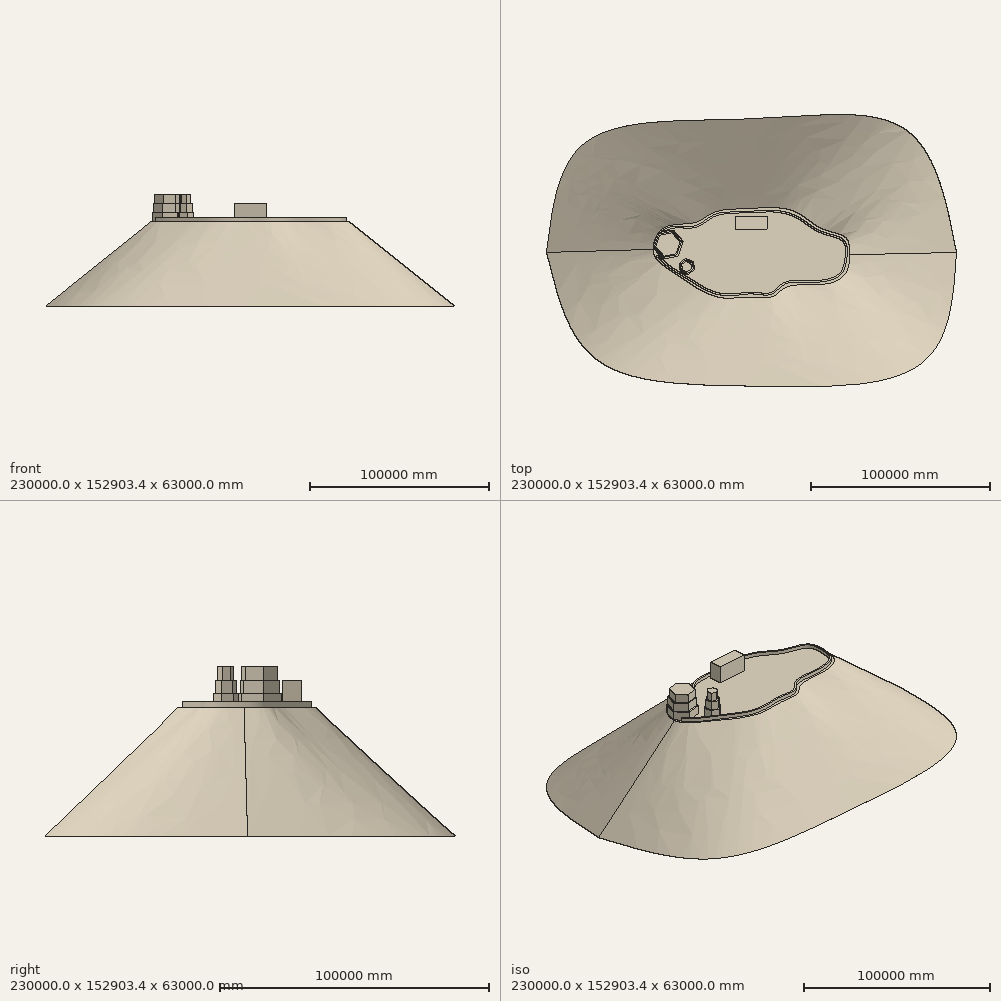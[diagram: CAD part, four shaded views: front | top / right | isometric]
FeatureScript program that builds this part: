
annotation { "Feature Type Name" : "Feature", "Feature Type Description" : "" }
export const myFeature = defineFeature(function(context is Context, id is Id, definition is map)
    precondition{}
    {
        {
            var Q0;
            Q0=qCreatedBy(makeId("Top.planeOp"),FACE);
            var sketch = newSketch(context, id + "F0", { "sketchPlane" : qUnion([Q0])});
            skFitSpline(sketch, "E0", {"points": [v(-115000, 0) * mm, v(-93084.68, 61512.1) * mm, v(0, 75000) * mm, v(86370.97, 68951.61) * mm, v(115000, 0) * mm], "startDerivative": vector(39435.94, 326168.34) * mm, "endDerivative": vector(68602.5, -351904.63) * mm});
            skFitSpline(sketch, "E1", {"points": [v(-115000, 0) * mm, v(-87459.68, -59697.58) * mm, v(0, -75000) * mm, v(96532.26, -61512.1) * mm, v(115000, 0) * mm], "startDerivative": vector(74357.8, -308446.07) * mm, "endDerivative": vector(20026.61, 322600.8) * mm});
            skSolve(sketch);
        }
        {
            var Q0;
            Q0=qCreatedBy(makeId("Top.planeOp"),FACE);
            cPlane(context, id + "F1", {"entities" : qUnion([Q0]), "cplaneType" : CPlaneType.OFFSET, "offset" : 48000 * mm, "width" : 150 * mm, "height" : 150 * mm});
        }
        {
            var Q0;
            Q0=qCreatedBy(id+"F1.planeOp",FACE);
            var sketch = newSketch(context, id + "F2", { "sketchPlane" : qUnion([Q0])});
            skFitSpline(sketch, "E2", {"points": [v(-55000, 0) * mm, v(-49195.48, 13593.62) * mm, v(-31440.72, 16737.7) * mm, v(-21638.61, 22101.1) * mm, v(0, 25000) * mm, v(24042.9, 23025.84) * mm, v(39023.49, 13593.62) * mm, v(52894.4, 8230.2) * mm, v(55000, 0) * mm, v(53449.23, -10819.18) * mm, v(43092.29, -17477.21) * mm, v(20159.05, -19326.67) * mm, v(12391.34, -24690.08) * mm, v(0, -25000) * mm, v(-19049.38, -25000) * mm, v(-45126.69, -10449.29) * mm, v(-55000, 0) * mm]});
            skSolve(sketch);
        }
        {
            var Q0;
            Q0=makeQuery(id+"F2.imprint","IMPRINT",FACE,{"disambiguationData":[TD([[makeQuery(id+"F2.imprint","IMPRINT",EDGE,{"derivedFrom":sQuery(id+"F2.wireOp",EDGE,"E2")}),-1.0]])]});
            var Q1;
            Q1=makeQuery(id+"F0.imprint","IMPRINT",FACE,{"disambiguationData":[TD([[makeQuery(id+"F0.imprint","IMPRINT",EDGE,{"derivedFrom":sQuery(id+"F0.wireOp",EDGE,"E0")}),-1.0]])]});
            loft(context, id + "F3", {"sheetProfilesArray" : [{ "sheetProfileEntities" : qUnion([Q0]) }, { "sheetProfileEntities" : qUnion([Q1]) }]});
        }
        {
            var Q0;
            Q0=makeQuery(id+"F3.opLoft","CAP_FACE",FACE,{"disambiguationData":[OSD([makeQuery(id+"F2.imprint","IMPRINT",FACE,{"disambiguationData":[TD([[makeQuery(id+"F2.imprint","IMPRINT",EDGE,{"derivedFrom":sQuery(id+"F2.wireOp",EDGE,"E2")}),-1.0]])]})])],"isStart":true});
            var sketch = newSketch(context, id + "F4", { "sketchPlane" : qUnion([Q0])});
            skLineSegment(sketch, "E3", {"start": v(-54550.48, 6198.7) * mm, "end": v(-46752.04, 4414.26) * mm});
            skCircle(sketch, "E4.cCircle", {"center": v(-46752.04, 4414.26) * mm, "radius": 7500 * mm, "construction": true});
            skLineSegment(sketch, "E4.0", {"start": v(-38242.25, 6021.6) * mm, "end": v(-41105.15, -2151.77) * mm});
            skLineSegment(sketch, "E4.1", {"start": v(-41105.15, -2151.77) * mm, "end": v(-49614.94, -3759.1) * mm});
            skLineSegment(sketch, "E4.2", {"start": v(-49614.94, -3759.1) * mm, "end": v(-55261.83, 2806.92) * mm});
            skLineSegment(sketch, "E4.3", {"start": v(-55261.83, 2806.92) * mm, "end": v(-52398.92, 10980.28) * mm});
            skLineSegment(sketch, "E4.4", {"start": v(-52398.92, 10980.28) * mm, "end": v(-43889.14, 12587.62) * mm});
            skLineSegment(sketch, "E4.5", {"start": v(-43889.14, 12587.62) * mm, "end": v(-38242.25, 6021.6) * mm});
            skPoint(sketch, "E4.0.midPoint", {"position": v(-39673.7, 1934.91) * mm});
            skSolve(sketch);
        }
        {
            var Q0;
            Q0=makeQuery(id+"F4.imprint","IMPRINT",FACE,{"disambiguationData":[TD([[makeQuery(id+"F4.imprint","IMPRINT",EDGE,{"derivedFrom":sQuery(id+"F4.wireOp",EDGE,"E4.0")}),-1.0]])]});
            extrude(context, id + "F5", {"entities" : qUnion([Q0]), "operationType" : NewBodyOperationType.ADD, "depth" : 5000 * mm});
        }
        {
            var Q0;
            Q0=makeQuery(id+"F5.opExtrude","CAP_FACE",FACE,{"disambiguationData":[OSD([sQuery(id+"F0.wireOp",EDGE,"E0"),sQuery(id+"F0.wireOp",EDGE,"E1"),sQuery(id+"F2.wireOp",EDGE,"E2"),sQuery(id+"F4.wireOp",EDGE,"E4.0"),sQuery(id+"F4.wireOp",EDGE,"E4.1"),sQuery(id+"F4.wireOp",EDGE,"E4.2"),sQuery(id+"F4.wireOp",EDGE,"E4.3"),sQuery(id+"F4.wireOp",EDGE,"E4.4"),sQuery(id+"F4.wireOp",EDGE,"E4.5")])],"isStart":false});
            var sketch = newSketch(context, id + "F6", { "sketchPlane" : qUnion([Q0])});
            skCircle(sketch, "E5.cCircle", {"center": v(-46880.17, 4500.61) * mm, "radius": 6688.06 * mm, "construction": true});
            skLineSegment(sketch, "E5.0", {"start": v(-54478.4, 3119.6) * mm, "end": v(-51875.28, 10390.35) * mm});
            skLineSegment(sketch, "E5.1", {"start": v(-51875.28, 10390.35) * mm, "end": v(-44277.06, 11771.37) * mm});
            skLineSegment(sketch, "E5.2", {"start": v(-44277.06, 11771.37) * mm, "end": v(-39281.95, 5881.63) * mm});
            skLineSegment(sketch, "E5.3", {"start": v(-39281.95, 5881.63) * mm, "end": v(-41885.06, -1389.13) * mm});
            skLineSegment(sketch, "E5.4", {"start": v(-41885.06, -1389.13) * mm, "end": v(-49483.28, -2770.15) * mm});
            skLineSegment(sketch, "E5.5", {"start": v(-49483.28, -2770.15) * mm, "end": v(-54478.4, 3119.6) * mm});
            skPoint(sketch, "E5.0.midPoint", {"position": v(-53176.84, 6754.97) * mm});
            skSolve(sketch);
        }
        {
            var Q0;
            Q0=makeQuery(id+"F6.imprint","IMPRINT",FACE,{"disambiguationData":[TD([[makeQuery(id+"F6.imprint","IMPRINT",EDGE,{"derivedFrom":sQuery(id+"F6.wireOp",EDGE,"E5.0")}),-1.0]])]});
            extrude(context, id + "F7", {"entities" : qUnion([Q0]), "operationType" : NewBodyOperationType.ADD, "depth" : 5000 * mm});
        }
        {
            var Q0;
            Q0=makeQuery(id+"F7.opExtrude","CAP_FACE",FACE,{"disambiguationData":[OSD([sQuery(id+"F6.wireOp",EDGE,"E5.0"),sQuery(id+"F6.wireOp",EDGE,"E5.1"),sQuery(id+"F6.wireOp",EDGE,"E5.2"),sQuery(id+"F6.wireOp",EDGE,"E5.3"),sQuery(id+"F6.wireOp",EDGE,"E5.4"),sQuery(id+"F6.wireOp",EDGE,"E5.5")])],"isStart":false});
            var sketch = newSketch(context, id + "F8", { "sketchPlane" : qUnion([Q0])});
            skCircle(sketch, "E6.cCircle", {"center": v(-46796.6, 4410.22) * mm, "radius": 6040.92 * mm, "construction": true});
            skLineSegment(sketch, "E6.0", {"start": v(-51393, 9657.15) * mm, "end": v(-44550.83, 11014.27) * mm});
            skLineSegment(sketch, "E6.1", {"start": v(-44550.83, 11014.27) * mm, "end": v(-39954.44, 5767.34) * mm});
            skLineSegment(sketch, "E6.2", {"start": v(-39954.44, 5767.34) * mm, "end": v(-42200.22, -836.7) * mm});
            skLineSegment(sketch, "E6.3", {"start": v(-42200.22, -836.7) * mm, "end": v(-49042.39, -2193.83) * mm});
            skLineSegment(sketch, "E6.4", {"start": v(-49042.39, -2193.83) * mm, "end": v(-53638.77, 3053.1) * mm});
            skLineSegment(sketch, "E6.5", {"start": v(-53638.77, 3053.1) * mm, "end": v(-51393, 9657.15) * mm});
            skPoint(sketch, "E6.0.midPoint", {"position": v(-47971.91, 10335.7) * mm});
            skSolve(sketch);
        }
        {
            var Q0;
            {var subQ0=sQuery(id+"F2.wireOp",EDGE,"E2");var subQ1=makeQuery(id+"F2.imprint","IMPRINT",EDGE,{"derivedFrom":subQ0});Q0=makeQuery(id+"F5.boolean.opBoolean","SPLIT",FACE,{"disambiguationData":[TD([makeQuery(id+"F5.opExtrude","SWEPT_FACE",FACE,{"disambiguationData":[OSD([sQuery(id+"F4.wireOp",EDGE,"E4.0")])]})])],"derivedFrom":makeQuery(id+"F3.opLoft","CAP_FACE",FACE,{"disambiguationData":[OSD([makeQuery(id+"F2.imprint","IMPRINT",FACE,{"disambiguationData":[TD([[subQ1,-1.0]])]})])],"isStart":true})});}
            var sketch = newSketch(context, id + "F9", { "sketchPlane" : qUnion([Q0])});
            skPoint(sketch, "E7.0.internal.snap0", {"position": v(-47955.39, 11819.58) * mm});
            skFitSpline(sketch, "E7", {"points": [v(-51090.18, 11819.58) * mm, v(-45135.25, 14330.4) * mm, v(-38003.08, 14696.04) * mm, v(-30275.62, 15385.9) * mm, v(-21578.99, 20754.82) * mm, v(-11237.18, 22930.05) * mm, v(4464.42, 23551.87) * mm, v(15659.1, 23396.88) * mm, v(26853.06, 19665.5) * mm, v(34781.74, 14145.25) * mm, v(42400.23, 10802.7) * mm, v(50252.3, 8083.85) * mm, v(53518.6, 3495.47) * mm, v(52973.57, -6376.8) * mm, v(49708.45, -12986.25) * mm, v(39213.22, -16561.05) * mm, v(28252.34, -16560.04) * mm, v(18612.73, -18035.92) * mm, v(13250, -22469.3) * mm, v(8040.3, -23946.46) * mm, v(0, -23245.23) * mm, v(-6185.77, -23867.9) * mm, v(-17612.52, -23868.43) * mm, v(-28573.08, -19514.87) * mm, v(-35958.38, -14850.08) * mm, v(-45018.89, -9321) * mm, v(-53569.9, -2091.5) * mm], "startDerivative": vector(158396.75, 66508.43) * mm, "endDerivative": vector(-197831.18, 185301.4) * mm});
            skFitSpline(sketch, "E8.0", {"points": [v(-50703.04, 10897.56) * mm, v(-50593.48, 10943.56) * mm, v(-50373.3, 11038.71) * mm, v(-50039.51, 11189.33) * mm, v(-49702.07, 11346.38) * mm, v(-49360.94, 11508.37) * mm, v(-49016.19, 11673.88) * mm, v(-48667.98, 11841.43) * mm, v(-48316.53, 12009.58) * mm, v(-47962.14, 12176.9) * mm, v(-47605.14, 12341.9) * mm, v(-47245.93, 12503.18) * mm, v(-46884.93, 12659.29) * mm, v(-46522.62, 12808.8) * mm, v(-46220, 12926.73) * mm, v(-45977.77, 13016.39) * mm, v(-45796.1, 13081.12) * mm, v(-45614.5, 13143.18) * mm, v(-45463.27, 13192.52) * mm, v(-45342.4, 13230.5) * mm, v(-45251.8, 13258.2) * mm, v(-45161.27, 13285.13) * mm, v(-45085.9, 13306.89) * mm, v(-45025.65, 13323.88) * mm, v(-44980.49, 13336.41) * mm, v(-44935.35, 13348.74) * mm, v(-44897.75, 13358.83) * mm, v(-44867.69, 13366.8) * mm, v(-44837.6, 13374.7) * mm, v(-44799.97, 13384.45) * mm, v(-44754.76, 13395.95) * mm, v(-44694.4, 13411.04) * mm, v(-44618.82, 13429.43) * mm, v(-44527.9, 13450.73) * mm, v(-44436.77, 13471.3) * mm, v(-44314.96, 13497.73) * mm, v(-44162.14, 13528.96) * mm, v(-43977.85, 13563.63) * mm, v(-43792.63, 13595.55) * mm, v(-43544.43, 13634.57) * mm, v(-43231.83, 13676.9) * mm, v(-42852.9, 13717.99) * mm, v(-42470.15, 13750.01) * mm, v(-42083.58, 13773.61) * mm, v(-41693.22, 13789.44) * mm, v(-41299.1, 13798.15) * mm, v(-40901.31, 13800.43) * mm, v(-40499.89, 13796.95) * mm, v(-40094.9, 13788.43) * mm, v(-39686.43, 13775.57) * mm, v(-39343.2, 13761.85) * mm, v(-39066.94, 13749.43) * mm, v(-38858.92, 13739.5) * mm, v(-38650.08, 13729.04) * mm, v(-38475.37, 13719.96) * mm, v(-38335.2, 13712.52) * mm, v(-38229.89, 13706.87) * mm, v(-38141.95, 13702.11) * mm, v(-38071.5, 13698.28) * mm, v(-38001, 13694.44) * mm, v(-37912.69, 13689.6) * mm, v(-37771.06, 13681.86) * mm, v(-37593.4, 13672.16) * mm, v(-37379.22, 13660.69) * mm, v(-37164.09, 13649.52) * mm, v(-36948.02, 13638.82) * mm, v(-36658.7, 13625.38) * mm, v(-36294.83, 13610.53) * mm, v(-35854.78, 13597.11) * mm, v(-35411.5, 13589.41) * mm, v(-34965.12, 13588.76) * mm, v(-34515.84, 13596.52) * mm, v(-34063.83, 13614.06) * mm, v(-33609.28, 13642.8) * mm, v(-33152.43, 13684.15) * mm, v(-32693.53, 13739.56) * mm, v(-32232.89, 13810.48) * mm, v(-31847.86, 13883.72) * mm, v(-31539.35, 13951.5) * mm, v(-31307.78, 14007.13) * mm, v(-31076.1, 14067.7) * mm, v(-30844.34, 14133.41) * mm, v(-30651.22, 14192.59) * mm, v(-30496.76, 14242.66) * mm, v(-30380.94, 14281.6) * mm, v(-30265.17, 14321.96) * mm, v(-30168.73, 14356.77) * mm, v(-30091.6, 14385.35) * mm, v(-30033.78, 14407.15) * mm, v(-29985.6, 14425.62) * mm, v(-29947.07, 14440.58) * mm, v(-29918.18, 14451.9) * mm, v(-29889.29, 14463.3) * mm, v(-29850.81, 14478.62) * mm, v(-29802.79, 14497.97) * mm, v(-29745.27, 14521.52) * mm, v(-29668.74, 14553.35) * mm, v(-29573.34, 14593.93) * mm, v(-29459.3, 14643.86) * mm, v(-29345.67, 14694.98) * mm, v(-29194.72, 14764.7) * mm, v(-29007.04, 14854.64) * mm, v(-28783.35, 14966.8) * mm, v(-28561.12, 15082.9) * mm, v(-28340.25, 15202.71) * mm, v(-28047.48, 15367.04) * mm, v(-27684.57, 15580.42) * mm, v(-27253.35, 15847.28) * mm, v(-26825.88, 16123.04) * mm, v(-26401.68, 16405.85) * mm, v(-25980.3, 16693.88) * mm, v(-25561.36, 16985.3) * mm, v(-25144.51, 17278.32) * mm, v(-24729.46, 17571.15) * mm, v(-24315.95, 17861.99) * mm, v(-23903.76, 18149.06) * mm, v(-23492.75, 18430.6) * mm, v(-23082.76, 18704.83) * mm, v(-22741.9, 18925.81) * mm, v(-22469.66, 19097.22) * mm, v(-22265.7, 19222.86) * mm, v(-22061.98, 19345.39) * mm, v(-21858.48, 19464.59) * mm, v(-21689.09, 19560.98) * mm, v(-21553.7, 19636.23) * mm, v(-21452.2, 19691.7) * mm, v(-21350.78, 19746.2) * mm, v(-21266.31, 19790.78) * mm, v(-21198.77, 19825.92) * mm, v(-21148.12, 19852.02) * mm, v(-21097.5, 19877.85) * mm, v(-21046.82, 19903.45) * mm, v(-20996.1, 19928.82) * mm, v(-20928.4, 19962.34) * mm, v(-20809.77, 20020.2) * mm, v(-20639.76, 20100.62) * mm, v(-20434.86, 20193.6) * mm, v(-20229, 20283.15) * mm, v(-20022.1, 20369.38) * mm, v(-19744.8, 20480) * mm, v(-19395.26, 20610.39) * mm, v(-18970.69, 20754.85) * mm, v(-18540.5, 20887.97) * mm, v(-18104.21, 21010.35) * mm, v(-17661.4, 21122.61) * mm, v(-17211.62, 21225.35) * mm, v(-16754.5, 21319.16) * mm, v(-16289.65, 21404.63) * mm, v(-15816.74, 21482.36) * mm, v(-15335.43, 21552.94) * mm, v(-14845.4, 21616.97) * mm, v(-14346.36, 21675.07) * mm, v(-13838.02, 21727.84) * mm, v(-13320.1, 21775.92) * mm, v(-12880.32, 21812.6) * mm, v(-12523.43, 21840.23) * mm, v(-12253.21, 21860.18) * mm, v(-11980.4, 21879.44) * mm, v(-11750.88, 21894.98) * mm, v(-11565.93, 21907.14) * mm, v(-11426.55, 21916.15) * mm, v(-11309.85, 21923.55) * mm, v(-11216.15, 21929.43) * mm, v(-11122.22, 21935.28) * mm, v(-11004.42, 21942.52) * mm, v(-10862.46, 21951.12) * mm, v(-10719.9, 21959.62) * mm, v(-10529.05, 21970.84) * mm, v(-10289.07, 21984.63) * mm, v(-9998.9, 22000.82) * mm, v(-9706.66, 22016.67) * mm, v(-9314.35, 22037.34) * mm, v(-8819.22, 22062.37) * mm, v(-8218.23, 22091.18) * mm, v(-7611.17, 22118.84) * mm, v(-6998.78, 22145.44) * mm, v(-6176.16, 22179.6) * mm, v(-5138.3, 22220.04) * mm, v(-3883.52, 22265.62) * mm, v(-2625.3, 22308.93) * mm, v(-1369.55, 22350.63) * mm, v(-330.07, 22384.6) * mm, v(494.4, 22411.62) * mm, v(1108.45, 22431.91) * mm, v(1717.48, 22452.3) * mm, v(2320.76, 22472.87) * mm, v(2818.1, 22490.24) * mm, v(3212.36, 22504.3) * mm, v(3506.17, 22514.96) * mm, v(3798, 22525.72) * mm, v(4039.45, 22534.79) * mm, v(4231.54, 22542.1) * mm, v(4351.13, 22546.71) * mm, v(4446.53, 22550.41) * mm, v(4517.93, 22553.2) * mm, v(4589.18, 22555.99) * mm, v(4683.97, 22559.72) * mm, v(4802.06, 22564.4) * mm, v(4990.18, 22571.92) * mm, v(5317.26, 22585.12) * mm, v(5778.58, 22603.95) * mm, v(6323.26, 22626.06) * mm, v(6859.6, 22647.23) * mm, v(7388.16, 22667.02) * mm, v(8083.31, 22690.95) * mm, v(8935.73, 22715.18) * mm, v(9936.94, 22731.67) * mm, v(10921.3, 22732.13) * mm, v(11893.83, 22713.17) * mm, v(12698.7, 22678.38) * mm, v(13341.88, 22637.47) * mm, v(13824.6, 22599.83) * mm, v(14308.33, 22554.8) * mm, v(14712.85, 22510.76) * mm, v(14997.06, 22476.32) * mm, v(15159.8, 22455.58) * mm, v(15282.05, 22439.5) * mm, v(15384.08, 22425.63) * mm, v(15465.8, 22414.27) * mm, v(15547.6, 22402.72) * mm, v(15650, 22387.93) * mm, v(15773.12, 22369.63) * mm, v(15896.5, 22350.76) * mm, v(16061.28, 22324.86) * mm, v(16267.82, 22291.1) * mm, v(16516.47, 22248.36) * mm, v(16848.95, 22188.43) * mm, v(17266.15, 22108.03) * mm, v(17768.71, 22002.88) * mm, v(18272.58, 21889.15) * mm, v(18945.31, 21726.2) * mm, v(19786.36, 21501.6) * mm, v(20790.89, 21199.46) * mm, v(21619.93, 20921.26) * mm, v(22275.86, 20683.34) * mm, v(22763.54, 20497.33) * mm, v(23246.34, 20303.89) * mm, v(23723.65, 20103.14) * mm, v(24194.84, 19895.23) * mm, v(24581.9, 19716.11) * mm, v(24887.86, 19569.37) * mm, v(25115.43, 19457.61) * mm, v(25341, 19344.17) * mm, v(25564.52, 19229.06) * mm, v(25749, 19131.77) * mm, v(25895.47, 19053.12) * mm, v(26004.75, 18993.73) * mm, v(26113.47, 18933.94) * mm, v(26221.6, 18873.75) * mm, v(26311.22, 18823.26) * mm, v(26382.6, 18782.67) * mm, v(26436.02, 18752.11) * mm, v(26489.33, 18721.44) * mm, v(26560.24, 18680.4) * mm, v(26683.92, 18608.19) * mm, v(26859.47, 18503.94) * mm, v(27068.38, 18377.19) * mm, v(27275.6, 18248.86) * mm, v(27481.2, 18119.03) * mm, v(27753.28, 17944.05) * mm, v(28089.73, 17722) * mm, v(28488.18, 17450.89) * mm, v(28881.92, 17175.8) * mm, v(29271.52, 16897.45) * mm, v(29786.26, 16522.85) * mm, v(30295.05, 16144.49) * mm, v(30800.25, 15765.21) * mm, v(31177.96, 15481.04) * mm, v(31555.1, 15197.88) * mm, v(31932.25, 14916.48) * mm, v(32310.07, 14637.6) * mm, v(32626, 14407.94) * mm, v(32879.7, 14226.25) * mm, v(33070.55, 14091.1) * mm, v(33262.04, 13957.17) * mm, v(33454.25, 13824.55) * mm, v(33647.28, 13693.36) * mm, v(33808.87, 13585.3) * mm, v(33938.64, 13499.67) * mm, v(34036.21, 13435.87) * mm, v(34117.75, 13383.06) * mm, v(34183.11, 13341.04) * mm, v(34224.02, 13314.87) * mm, v(34256.79, 13294) * mm, v(34289.56, 13273.16) * mm, v(34330.56, 13247.2) * mm, v(34379.79, 13216.2) * mm, v(34445.48, 13175.03) * mm, v(34527.7, 13123.9) * mm, v(34626.5, 13063.1) * mm, v(34725.48, 13002.82) * mm, v(34857.64, 12923.15) * mm, v(35023.24, 12824.88) * mm, v(35222.6, 12709) * mm, v(35422.6, 12595.17) * mm, v(35623.26, 12483.32) * mm, v(35891.68, 12336.8) * mm, v(36228.86, 12158.49) * mm, v(36636.2, 11951.94) * mm, v(37046.3, 11752.56) * mm, v(37459.24, 11560.07) * mm, v(37875.08, 11374.19) * mm, v(38433.49, 11134.77) * mm, v(38997.95, 10907.43) * mm, v(39568.78, 10691.01) * mm, v(40000.15, 10533.87) * mm, v(40362.42, 10406.98) * mm, v(40653.95, 10307.76) * mm, v(40873.46, 10234.46) * mm, v(41093.86, 10162.23) * mm, v(41315.14, 10091.04) * mm, v(41537.33, 10020.84) * mm, v(41723.25, 9963.15) * mm, v(41872.45, 9917.46) * mm, v(41965.89, 9889.1) * mm, v(42040.76, 9866.52) * mm, v(42096.97, 9849.63) * mm, v(42153.24, 9832.8) * mm, v(42228.3, 9810.46) * mm, v(42322.22, 9782.66) * mm, v(42472.61, 9738.5) * mm, v(42660.83, 9683.81) * mm, v(42886.92, 9618.94) * mm, v(43113.11, 9554.7) * mm, v(43339.28, 9491.03) * mm, v(43640.63, 9406.72) * mm, v(44016.59, 9302.23) * mm, v(44465.5, 9177.52) * mm, v(44911.11, 9052.76) * mm, v(45352.29, 8927.24) * mm, v(45787.9, 8800.28) * mm, v(46216.82, 8671.22) * mm, v(46637.88, 8539.4) * mm, v(47049.89, 8404.25) * mm, v(47451.65, 8265.18) * mm, v(47841.96, 8121.65) * mm, v(48219.59, 7973.18) * mm, v(48522.7, 7845) * mm, v(48757.63, 7739.59) * mm, v(48929.9, 7659.06) * mm, v(49098.1, 7577.03) * mm, v(49262.08, 7493.47) * mm, v(49395.1, 7422.55) * mm, v(49499.27, 7365.02) * mm, v(49576.25, 7321.48) * mm, v(49639.44, 7284.86) * mm, v(49689.4, 7255.37) * mm, v(49726.59, 7233.15) * mm, v(49763.47, 7210.83) * mm, v(49800.1, 7188.4) * mm, v(49836.46, 7165.83) * mm, v(49884.58, 7135.6) * mm, v(49944.08, 7097.5) * mm, v(50014.43, 7051.3) * mm, v(50083.73, 7004.63) * mm, v(50174.74, 6941.74) * mm, v(50285.93, 6861.9) * mm, v(50458.4, 6731.53) * mm, v(50663.98, 6563.48) * mm, v(50895.18, 6353.33) * mm, v(51111.47, 6134.2) * mm, v(51313.42, 5905.47) * mm, v(51501.61, 5666.38) * mm, v(51676.52, 5416.08) * mm, v(51838.55, 5153.63) * mm, v(51987.97, 4878.04) * mm, v(52102.1, 4636.6) * mm, v(52187.2, 4435.89) * mm, v(52247.9, 4281.47) * mm, v(52305.48, 4123.04) * mm, v(52359.9, 3960.51) * mm, v(52402.62, 3821.56) * mm, v(52435.19, 3708.25) * mm, v(52458.8, 3622.18) * mm, v(52481.62, 3535.01) * mm, v(52499.95, 3461.45) * mm, v(52514.21, 3402.03) * mm, v(52524.7, 3357.2) * mm, v(52534.99, 3312.07) * mm, v(52545.07, 3266.67) * mm, v(52554.94, 3220.96) * mm, v(52567.85, 3159.58) * mm, v(52583.49, 3082.08) * mm, v(52601.45, 2987.86) * mm, v(52624.35, 2860.63) * mm, v(52650.97, 2698.68) * mm, v(52679.75, 2499.87) * mm, v(52705.38, 2296.8) * mm, v(52727.87, 2089.68) * mm, v(52747.26, 1878.72) * mm, v(52769.03, 1592.6) * mm, v(52788.7, 1226.36) * mm, v(52800.59, 774.77) * mm, v(52801.23, 312.65) * mm, v(52791.1, -158.47) * mm, v(52770.7, -637.07) * mm, v(52740.62, -1121.66) * mm, v(52701.38, -1610.78) * mm, v(52653.58, -2102.97) * mm, v(52597.8, -2596.8) * mm, v(52534.65, -3090.87) * mm, v(52464.74, -3583.76) * mm, v(52388.68, -4074.1) * mm, v(52307.1, -4560.48) * mm, v(52235.03, -4961.36) * mm, v(52175.23, -5278.72) * mm, v(52137.03, -5475.54) * mm, v(52106.02, -5631.98) * mm, v(52082.54, -5748.8) * mm, v(52058.86, -5865.05) * mm, v(52038.96, -5961.46) * mm, v(52022.94, -6038.3) * mm, v(52010.88, -6095.77) * mm, v(52000.8, -6143.54) * mm, v(51992.7, -6181.68) * mm, v(51984.6, -6219.75) * mm, v(51974.46, -6267.21) * mm, v(51958.17, -6342.88) * mm, v(51937.72, -6436.94) * mm, v(51913.01, -6549) * mm, v(51879.81, -6697.3) * mm, v(51837.81, -6880.62) * mm, v(51786.48, -7097.26) * mm, v(51734.09, -7310.55) * mm, v(51680.5, -7520.47) * mm, v(51607.33, -7795.85) * mm, v(51512.3, -8131.57) * mm, v(51391.66, -8520.77) * mm, v(51263.52, -8896.26) * mm, v(51127, -9258.1) * mm, v(50981.28, -9606.43) * mm, v(50825.46, -9941.5) * mm, v(50658.67, -10263.63) * mm, v(50479.94, -10573.32) * mm, v(50288.2, -10871.15) * mm, v(50116.6, -11110.01) * mm, v(49971.55, -11295.85) * mm, v(49858.69, -11432.7) * mm, v(49741.57, -11567.1) * mm, v(49620, -11699.15) * mm, v(49514.79, -11807.28) * mm, v(49428.18, -11892.68) * mm, v(49361.98, -11956.2) * mm, v(49294.5, -12019.16) * mm, v(49225.7, -12081.6) * mm, v(49167.27, -12133.2) * mm, v(49119.84, -12174.22) * mm, v(49083.93, -12204.86) * mm, v(49047.67, -12235.36) * mm, v(49011, -12265.78) * mm, v(48973.96, -12296.1) * mm, v(48924.03, -12336.43) * mm, v(48860.66, -12386.59) * mm, v(48783.07, -12446.4) * mm, v(48703.95, -12505.82) * mm, v(48596.46, -12584.51) * mm, v(48458.38, -12681.84) * mm, v(48286.9, -12796.92) * mm, v(48109.8, -12910.21) * mm, v(47927.22, -13021.65) * mm, v(47676.74, -13167.68) * mm, v(47350.84, -13345.3) * mm, v(46940.7, -13550.22) * mm, v(46512.93, -13746.58) * mm, v(46068.98, -13934.16) * mm, v(45610.31, -14112.75) * mm, v(45138.38, -14282.21) * mm, v(44654.62, -14442.41) * mm, v(44160.48, -14593.28) * mm, v(43657.4, -14734.75) * mm, v(43146.8, -14866.77) * mm, v(42630.1, -14989.34) * mm, v(42108.75, -15102.43) * mm, v(41584.12, -15206.07) * mm, v(41057.65, -15300.26) * mm, v(40618.55, -15370.9) * mm, v(40267.75, -15422.71) * mm, v(40005.07, -15459.23) * mm, v(39742.98, -15493.42) * mm, v(39525.22, -15519.96) * mm, v(39351.48, -15540.04) * mm, v(39243.1, -15552.1) * mm, v(39156.55, -15561.46) * mm, v(39070.09, -15570.63) * mm, v(38919.01, -15586.17) * mm, v(38703.82, -15606.96) * mm, v(38446.55, -15629.72) * mm, v(38190.19, -15650.37) * mm, v(37849.51, -15675.17) * mm, v(37425.68, -15701.24) * mm, v(36919.92, -15725.2) * mm, v(36416.6, -15742.38) * mm, v(35915.34, -15753.36) * mm, v(35249.25, -15760.48) * mm, v(34419.92, -15756.67) * mm, v(33427.07, -15736.34) * mm, v(32433.74, -15704.8) * mm, v(31603.28, -15673.08) * mm, v(30935.98, -15646.78) * mm, v(30433.7, -15627.2) * mm, v(29929.3, -15608.37) * mm, v(29506.93, -15593.8) * mm, v(29167.66, -15583.13) * mm, v(28912.48, -15575.69) * mm, v(28656.53, -15568.9) * mm, v(28442.57, -15563.83) * mm, v(28270.99, -15560.18) * mm, v(28099.1, -15556.8) * mm, v(27883.71, -15553.14) * mm, v(27624.5, -15549.72) * mm, v(27364.61, -15547.37) * mm, v(27104.18, -15546.18) * mm, v(26756.34, -15546.28) * mm, v(26320.64, -15549.78) * mm, v(25797.16, -15560.16) * mm, v(25273.82, -15577.5) * mm, v(24751.37, -15602.57) * mm, v(24230.56, -15636.18) * mm, v(23712.14, -15679.14) * mm, v(23196.84, -15732.3) * mm, v(22685.39, -15796.48) * mm, v(22178.51, -15872.6) * mm, v(21676.93, -15961.53) * mm, v(21181.37, -16064.24) * mm, v(20692.59, -16181.7) * mm, v(20211.33, -16314.9) * mm, v(19817.23, -16439.92) * mm, v(19506.54, -16548.88) * mm, v(19275.93, -16635.22) * mm, v(19047.84, -16726.31) * mm, v(18859.98, -16806.3) * mm, v(18711.08, -16872.82) * mm, v(18600.1, -16923.98) * mm, v(18489.87, -16976.44) * mm, v(18398.63, -17021.25) * mm, v(18326.02, -17057.77) * mm, v(18271.75, -17085.49) * mm, v(18217.68, -17113.55) * mm, v(18172.79, -17137.21) * mm, v(18136.97, -17156.32) * mm, v(18101.24, -17175.52) * mm, v(18056.78, -17199.7) * mm, v(18003.72, -17229) * mm, v(17950.97, -17258.56) * mm, v(17898.53, -17288.4) * mm, v(17829, -17328.51) * mm, v(17742.82, -17379.3) * mm, v(17640.58, -17441.22) * mm, v(17539.5, -17504.07) * mm, v(17439.54, -17567.8) * mm, v(17307.76, -17653.9) * mm, v(17145.77, -17763.53) * mm, v(16955.62, -17897.94) * mm, v(16707.51, -18080.53) * mm, v(16407.13, -18314.3) * mm, v(16060.94, -18601.13) * mm, v(15727.66, -18891.9) * mm, v(15405.97, -19184.25) * mm, v(15094.6, -19475.9) * mm, v(14792.36, -19764.65) * mm, v(14498.14, -20048.26) * mm, v(14210.9, -20324.57) * mm, v(13976.62, -20546.95) * mm, v(13791.84, -20719.07) * mm, v(13654.49, -20845.01) * mm, v(13518.3, -20967.55) * mm, v(13383.2, -21086.43) * mm, v(13249.13, -21201.4) * mm, v(13116.03, -21312.26) * mm, v(12983.85, -21418.75) * mm, v(12885.38, -21495.19) * mm, v(12820, -21544.66) * mm, v(12787.35, -21569.1) * mm, v(12754.76, -21593.23) * mm, v(12722.23, -21617.05) * mm, v(12695.15, -21636.65) * mm, v(12673.52, -21652.17) * mm, v(12651.9, -21667.59) * mm, v(12624.85, -21686.7) * mm, v(12592.35, -21709.4) * mm, v(12559.81, -21731.84) * mm, v(12516.38, -21761.44) * mm, v(12461.98, -21797.81) * mm, v(12396.53, -21840.5) * mm, v(12309.02, -21896.12) * mm, v(12199.15, -21963.28) * mm, v(12066.43, -22040.17) * mm, v(11932.74, -22113.46) * mm, v(11753.06, -22206.47) * mm, v(11525.53, -22314.15) * mm, v(11246.94, -22430.2) * mm, v(10961.93, -22533.64) * mm, v(10669.62, -22624.89) * mm, v(10369.19, -22704.29) * mm, v(10059.86, -22772.14) * mm, v(9740.92, -22828.66) * mm, v(9466.62, -22866.5) * mm, v(9241.77, -22891.29) * mm, v(9070.38, -22907.16) * mm, v(8896.17, -22920.35) * mm, v(8719.08, -22930.85) * mm, v(8539.07, -22938.71) * mm, v(8386.58, -22943.07) * mm, v(8263.07, -22945.26) * mm, v(8169.68, -22946.25) * mm, v(8091.22, -22946.54) * mm, v(8028.07, -22946.45) * mm, v(7964.63, -22946.15) * mm, v(7884.78, -22945.38) * mm, v(7755.9, -22943.32) * mm, v(7592.77, -22939.23) * mm, v(7393.92, -22932.02) * mm, v(7124.93, -22919.46) * mm, v(6781.92, -22898.56) * mm, v(6360.87, -22866.15) * mm, v(5931.75, -22827.41) * mm, v(5495.87, -22783.4) * mm, v(5054.49, -22735.2) * mm, v(4608.84, -22683.9) * mm, v(4160.1, -22630.6) * mm, v(3709.43, -22576.4) * mm, v(3257.92, -22522.43) * mm, v(2806.65, -22469.82) * mm, v(2356.65, -22419.72) * mm, v(1908.92, -22373.3) * mm, v(1538.48, -22338.63) * mm, v(1244.18, -22313.92) * mm, v(1024.58, -22297.05) * mm, v(806.22, -22282) * mm, v(625.36, -22271.1) * mm, v(481.38, -22263.44) * mm, v(373.76, -22258.26) * mm, v(266.52, -22253.64) * mm, v(177.48, -22250.3) * mm, v(106.44, -22247.93) * mm, v(53.27, -22246.31) * mm, v(0.2, -22244.85) * mm, v(-52.71, -22243.56) * mm, v(-105.45, -22242.42) * mm, v(-175.54, -22241.12) * mm, v(-297.63, -22239.4) * mm, v(-470.47, -22238.48) * mm, v(-675.5, -22239.78) * mm, v(-878.28, -22243.37) * mm, v(-1078.98, -22249.16) * mm, v(-1277.73, -22257.06) * mm, v(-1540.32, -22270.25) * mm, v(-1864.45, -22291.5) * mm, v(-2248.02, -22323.81) * mm, v(-2627.48, -22362.09) * mm, v(-3004.17, -22405.52) * mm, v(-3379.48, -22453.3) * mm, v(-3754.86, -22504.66) * mm, v(-4131.83, -22558.82) * mm, v(-4511.97, -22615.06) * mm, v(-4896.9, -22672.69) * mm, v(-5223.05, -22721.3) * mm, v(-5488.05, -22760.2) * mm, v(-5689.05, -22789.31) * mm, v(-5858.6, -22813.45) * mm, v(-5995.6, -22832.65) * mm, v(-6099.04, -22846.98) * mm, v(-6185.84, -22858.85) * mm, v(-6255.66, -22868.31) * mm, v(-6308.22, -22875.38) * mm, v(-6360.97, -22882.43) * mm, v(-6431.6, -22891.8) * mm, v(-6520.4, -22903.45) * mm, v(-6627.8, -22917.32) * mm, v(-6772.07, -22935.68) * mm, v(-6954.43, -22958.32) * mm, v(-7176.36, -22984.95) * mm, v(-7401.3, -23010.98) * mm, v(-7629.15, -23036.34) * mm, v(-7936.7, -23069.17) * mm, v(-8327.9, -23108.22) * mm, v(-8807.35, -23151.4) * mm, v(-9458.9, -23203.36) * mm, v(-10294.3, -23256.56) * mm, v(-11323.76, -23297.54) * mm, v(-12198.64, -23309.31) * mm, v(-12905.42, -23303.34) * mm, v(-13438.1, -23290.68) * mm, v(-13972.55, -23269.35) * mm, v(-14507.93, -23238.88) * mm, v(-15043.4, -23198.79) * mm, v(-15578.11, -23148.61) * mm, v(-16022.39, -23098.02) * mm, v(-16376.59, -23052.05) * mm, v(-16641.53, -23014.77) * mm, v(-16861.63, -22981.32) * mm, v(-17037.25, -22953.1) * mm, v(-17168.72, -22931.21) * mm, v(-17278.07, -22912.35) * mm, v(-17365.41, -22896.88) * mm, v(-17430.85, -22885.1) * mm, v(-17496.22, -22873.12) * mm, v(-17583.35, -22856.89) * mm, v(-17692.16, -22836.12) * mm, v(-17822.57, -22810.43) * mm, v(-17996.23, -22775.18) * mm, v(-18212.9, -22729.25) * mm, v(-18472.21, -22671.2) * mm, v(-18817, -22590) * mm, v(-19246.1, -22481.54) * mm, v(-19757.78, -22340.75) * mm, v(-20265.98, -22189.85) * mm, v(-20770.47, -22029.4) * mm, v(-21270.99, -21859.93) * mm, v(-21932.74, -21622.67) * mm, v(-22748.8, -21306.26) * mm, v(-23708.33, -20899.27) * mm, v(-24646.16, -20469.43) * mm, v(-25408, -20095.92) * mm, v(-26004.71, -19790.19) * mm, v(-26445.63, -19557.98) * mm, v(-26879.7, -19323.45) * mm, v(-27235.53, -19126.53) * mm, v(-27516.54, -18968.39) * mm, v(-27725.44, -18849.55) * mm, v(-27897.95, -18750.4) * mm, v(-28035, -18671.02) * mm, v(-28171.41, -18591.63) * mm, v(-28340.73, -18492.37) * mm, v(-28609.23, -18333.5) * mm, v(-28940.59, -18134.78) * mm, v(-29332.18, -17896.06) * mm, v(-29718.54, -17657.02) * mm, v(-30100.45, -17417.63) * mm, v(-30604.79, -17097.9) * mm, v(-31228.03, -16697.09) * mm, v(-31846.86, -16294.53) * mm, v(-32342.36, -15971.33) * mm, v(-32714.95, -15728.35) * mm, v(-33089.26, -15484.77) * mm, v(-33466.04, -15240.58) * mm, v(-33846.03, -14995.8) * mm, v(-34165.99, -14791.32) * mm, v(-34424.3, -14627.45) * mm, v(-34619.29, -14504.41) * mm, v(-34815.63, -14381.23) * mm, v(-34980.46, -14278.46) * mm, v(-35113.09, -14196.18) * mm, v(-35212.95, -14134.44) * mm, v(-35313.22, -14072.66) * mm, v(-35397.13, -14021.16) * mm, v(-35464.47, -13979.94) * mm, v(-35531.92, -13938.72) * mm, v(-35616.44, -13887.22) * mm, v(-35718.2, -13825.44) * mm, v(-35854.28, -13743.08) * mm, v(-36025.17, -13640.16) * mm, v(-36231.42, -13516.67) * mm, v(-36438.8, -13393.16) * mm, v(-36716.71, -13228.43) * mm, v(-37066.62, -13022.33) * mm, v(-37490.04, -12774.49) * mm, v(-37916.53, -12525.9) * mm, v(-38488.62, -12193.2) * mm, v(-39208.96, -11774.39) * mm, v(-40077.84, -11265.5) * mm, v(-40802.35, -10834.85) * mm, v(-41380.25, -10485.6) * mm, v(-41812.31, -10221.12) * mm, v(-42242.53, -9953.9) * mm, v(-42670.39, -9683.77) * mm, v(-43095.4, -9410.55) * mm, v(-43446.78, -9180.14) * mm, v(-43725.95, -8994.1) * mm, v(-43934.31, -8853.69) * mm, v(-44107.04, -8735.92) * mm, v(-44244.64, -8641.25) * mm, v(-44330.4, -8581.89) * mm, v(-44398.85, -8534.28) * mm, v(-44450.11, -8498.51) * mm, v(-44501.3, -8462.68) * mm, v(-44569.49, -8414.81) * mm, v(-44654.56, -8354.8) * mm, v(-44790.38, -8258.39) * mm, v(-44959.57, -8137.17) * mm, v(-45161.73, -7990.6) * mm, v(-45363.03, -7842.93) * mm, v(-45630.33, -7644.57) * mm, v(-45962.5, -7393.93) * mm, v(-46358.2, -7088.95) * mm, v(-46751.28, -6779.85) * mm, v(-47141.96, -6466.73) * mm, v(-47660.02, -6044.03) * mm, v(-48302.9, -5506.15) * mm, v(-49068.81, -4846.33) * mm, v(-49831.2, -4173.02) * mm, v(-50592.05, -3487.12) * mm, v(-51607.1, -2557.02) * mm, v(-52372.05, -1843.33) * mm, v(-52886.3, -1361.66) * mm]});
            skLineSegment(sketch, "E9", {"start": v(-47270.8, 12491.21) * mm, "end": v(-51090.18, 11819.58) * mm});
            skLineSegment(sketch, "E10", {"start": v(-53569.9, -2091.5) * mm, "end": v(-52886.3, -1361.66) * mm});
            skSolve(sketch);
        }
        {
            var Q0;
            Q0=makeQuery(id+"F9.imprint","IMPRINT",FACE,{"disambiguationData":[TD([[makeQuery(id+"F9.imprint","IMPRINT",EDGE,{"derivedFrom":sQuery(id+"F9.wireOp",EDGE,"E7")}),-1.0]])]});
            extrude(context, id + "F10", {"entities" : qUnion([Q0]), "operationType" : NewBodyOperationType.ADD, "depth" : 2000 * mm});
        }
        {
            var Q0;
            Q0=makeQuery(id+"F8.imprint","IMPRINT",FACE,{"disambiguationData":[TD([[makeQuery(id+"F8.imprint","IMPRINT",EDGE,{"derivedFrom":sQuery(id+"F8.wireOp",EDGE,"E6.0")}),-1.0]])]});
            extrude(context, id + "F11", {"entities" : qUnion([Q0]), "operationType" : NewBodyOperationType.ADD, "depth" : 5000 * mm});
        }
        {
            var Q0;
            {var subQ0=sQuery(id+"F2.wireOp",EDGE,"E2");var subQ1=makeQuery(id+"F2.imprint","IMPRINT",EDGE,{"derivedFrom":subQ0});Q0=makeQuery(id+"F5.boolean.opBoolean","SPLIT",FACE,{"disambiguationData":[TD([makeQuery(id+"F5.opExtrude","SWEPT_FACE",FACE,{"disambiguationData":[OSD([sQuery(id+"F4.wireOp",EDGE,"E4.0")])]})])],"derivedFrom":makeQuery(id+"F3.opLoft","CAP_FACE",FACE,{"disambiguationData":[OSD([makeQuery(id+"F2.imprint","IMPRINT",FACE,{"disambiguationData":[TD([[subQ1,-1.0]])]})])],"isStart":true})});}
            var sketch = newSketch(context, id + "F12", { "sketchPlane" : qUnion([Q0])});
            skCircle(sketch, "E11.cCircle", {"center": v(-36239.68, -8019.9) * mm, "radius": 4030.64 * mm, "construction": true});
            skLineSegment(sketch, "E11.0", {"start": v(-32591.87, -5129.4) * mm, "end": v(-31912.54, -9733.75) * mm});
            skLineSegment(sketch, "E11.1", {"start": v(-31912.54, -9733.75) * mm, "end": v(-35560.35, -12624.23) * mm});
            skLineSegment(sketch, "E11.2", {"start": v(-35560.35, -12624.23) * mm, "end": v(-39887.49, -10910.38) * mm});
            skLineSegment(sketch, "E11.3", {"start": v(-39887.49, -10910.38) * mm, "end": v(-40566.82, -6306.04) * mm});
            skLineSegment(sketch, "E11.4", {"start": v(-40566.82, -6306.04) * mm, "end": v(-36919, -3415.56) * mm});
            skLineSegment(sketch, "E11.5", {"start": v(-36919, -3415.56) * mm, "end": v(-32591.87, -5129.4) * mm});
            skPoint(sketch, "E11.0.midPoint", {"position": v(-32252.2, -7431.58) * mm});
            skSolve(sketch);
        }
        {
            var Q0;
            Q0=makeQuery(id+"F12.imprint","IMPRINT",FACE,{"disambiguationData":[TD([[makeQuery(id+"F12.imprint","IMPRINT",EDGE,{"derivedFrom":sQuery(id+"F12.wireOp",EDGE,"E11.0")}),-1.0]])]});
            extrude(context, id + "F13", {"entities" : qUnion([Q0]), "operationType" : NewBodyOperationType.ADD, "depth" : 5000 * mm});
        }
        {
            var Q0;
            Q0=makeQuery(id+"F13.opExtrude","CAP_FACE",FACE,{"disambiguationData":[OSD([sQuery(id+"F12.wireOp",EDGE,"E11.0"),sQuery(id+"F12.wireOp",EDGE,"E11.1"),sQuery(id+"F12.wireOp",EDGE,"E11.2"),sQuery(id+"F12.wireOp",EDGE,"E11.3"),sQuery(id+"F12.wireOp",EDGE,"E11.4"),sQuery(id+"F12.wireOp",EDGE,"E11.5")])],"isStart":false});
            var sketch = newSketch(context, id + "F14", { "sketchPlane" : qUnion([Q0])});
            skCircle(sketch, "E12.cCircle", {"center": v(-36239.68, -8150.63) * mm, "radius": 3399.16 * mm, "construction": true});
            skLineSegment(sketch, "E12.0", {"start": v(-36743.86, -4258.14) * mm, "end": v(-33120.77, -5767.76) * mm});
            skLineSegment(sketch, "E12.1", {"start": v(-33120.77, -5767.76) * mm, "end": v(-32616.6, -9660.25) * mm});
            skLineSegment(sketch, "E12.2", {"start": v(-32616.6, -9660.25) * mm, "end": v(-35735.5, -12043.12) * mm});
            skLineSegment(sketch, "E12.3", {"start": v(-35735.5, -12043.12) * mm, "end": v(-39358.59, -10533.5) * mm});
            skLineSegment(sketch, "E12.4", {"start": v(-39358.59, -10533.5) * mm, "end": v(-39862.77, -6641.02) * mm});
            skLineSegment(sketch, "E12.5", {"start": v(-39862.77, -6641.02) * mm, "end": v(-36743.86, -4258.14) * mm});
            skPoint(sketch, "E12.0.midPoint", {"position": v(-34932.32, -5012.95) * mm});
            skSolve(sketch);
        }
        {
            var Q0;
            Q0=makeQuery(id+"F14.imprint","IMPRINT",FACE,{"disambiguationData":[TD([[makeQuery(id+"F14.imprint","IMPRINT",EDGE,{"derivedFrom":sQuery(id+"F14.wireOp",EDGE,"E12.0")}),-1.0]])]});
            extrude(context, id + "F15", {"entities" : qUnion([Q0]), "operationType" : NewBodyOperationType.ADD, "depth" : 5000 * mm});
        }
        {
            var Q0;
            Q0=makeQuery(id+"F15.opExtrude","CAP_FACE",FACE,{"disambiguationData":[OSD([sQuery(id+"F14.wireOp",EDGE,"E12.0"),sQuery(id+"F14.wireOp",EDGE,"E12.1"),sQuery(id+"F14.wireOp",EDGE,"E12.2"),sQuery(id+"F14.wireOp",EDGE,"E12.3"),sQuery(id+"F14.wireOp",EDGE,"E12.4"),sQuery(id+"F14.wireOp",EDGE,"E12.5")])],"isStart":false});
            var sketch = newSketch(context, id + "F16", { "sketchPlane" : qUnion([Q0])});
            skCircle(sketch, "E13.cCircle", {"center": v(-36370.42, -8085.26) * mm, "radius": 2603.82 * mm, "construction": true});
            skLineSegment(sketch, "E13.0", {"start": v(-33981.28, -6259.94) * mm, "end": v(-33595.07, -9241.66) * mm});
            skLineSegment(sketch, "E13.1", {"start": v(-33595.07, -9241.66) * mm, "end": v(-35984.2, -11066.98) * mm});
            skLineSegment(sketch, "E13.2", {"start": v(-35984.2, -11066.98) * mm, "end": v(-38759.56, -9910.59) * mm});
            skLineSegment(sketch, "E13.3", {"start": v(-38759.56, -9910.59) * mm, "end": v(-39145.77, -6928.87) * mm});
            skLineSegment(sketch, "E13.4", {"start": v(-39145.77, -6928.87) * mm, "end": v(-36756.63, -5103.54) * mm});
            skLineSegment(sketch, "E13.5", {"start": v(-36756.63, -5103.54) * mm, "end": v(-33981.28, -6259.94) * mm});
            skPoint(sketch, "E13.0.midPoint", {"position": v(-33788.17, -7750.8) * mm});
            skSolve(sketch);
        }
        {
            var Q0;
            Q0=makeQuery(id+"F16.imprint","IMPRINT",FACE,{"disambiguationData":[TD([[makeQuery(id+"F16.imprint","IMPRINT",EDGE,{"derivedFrom":sQuery(id+"F16.wireOp",EDGE,"E13.0")}),-1.0]])]});
            extrude(context, id + "F17", {"entities" : qUnion([Q0]), "operationType" : NewBodyOperationType.ADD, "depth" : 5000 * mm});
        }
        {
            var Q0;
            {var subQ0=sQuery(id+"F2.wireOp",EDGE,"E2");var subQ1=makeQuery(id+"F2.imprint","IMPRINT",EDGE,{"derivedFrom":subQ0});Q0=makeQuery(id+"F5.boolean.opBoolean","SPLIT",FACE,{"disambiguationData":[TD([makeQuery(id+"F5.opExtrude","SWEPT_FACE",FACE,{"disambiguationData":[OSD([sQuery(id+"F4.wireOp",EDGE,"E4.0")])]})])],"derivedFrom":makeQuery(id+"F3.opLoft","CAP_FACE",FACE,{"disambiguationData":[OSD([makeQuery(id+"F2.imprint","IMPRINT",FACE,{"disambiguationData":[TD([[subQ1,-1.0]])]})])],"isStart":true})});}
            var sketch = newSketch(context, id + "F18", { "sketchPlane" : qUnion([Q0])});
            skLineSegment(sketch, "E14.bottom", {"start": v(-9244.49, 20247.9) * mm, "end": v(9244.49, 20247.9) * mm});
            skLineSegment(sketch, "E14.top", {"start": v(-9244.49, 13037.2) * mm, "end": v(9244.49, 13037.2) * mm});
            skLineSegment(sketch, "E14.left", {"start": v(-9244.49, 20247.9) * mm, "end": v(-9244.49, 13037.2) * mm});
            skLineSegment(sketch, "E14.right", {"start": v(9244.49, 20247.9) * mm, "end": v(9244.49, 13037.2) * mm});
            skSolve(sketch);
        }
        {
            var Q0;
            Q0=makeQuery(id+"F18.imprint","IMPRINT",FACE,{"disambiguationData":[TD([[makeQuery(id+"F18.imprint","IMPRINT",EDGE,{"derivedFrom":sQuery(id+"F18.wireOp",EDGE,"E14.bottom")}),-1.0]])]});
            extrude(context, id + "F19", {"entities" : qUnion([Q0]), "operationType" : NewBodyOperationType.ADD, "depth" : 10000 * mm});
        }
    });
